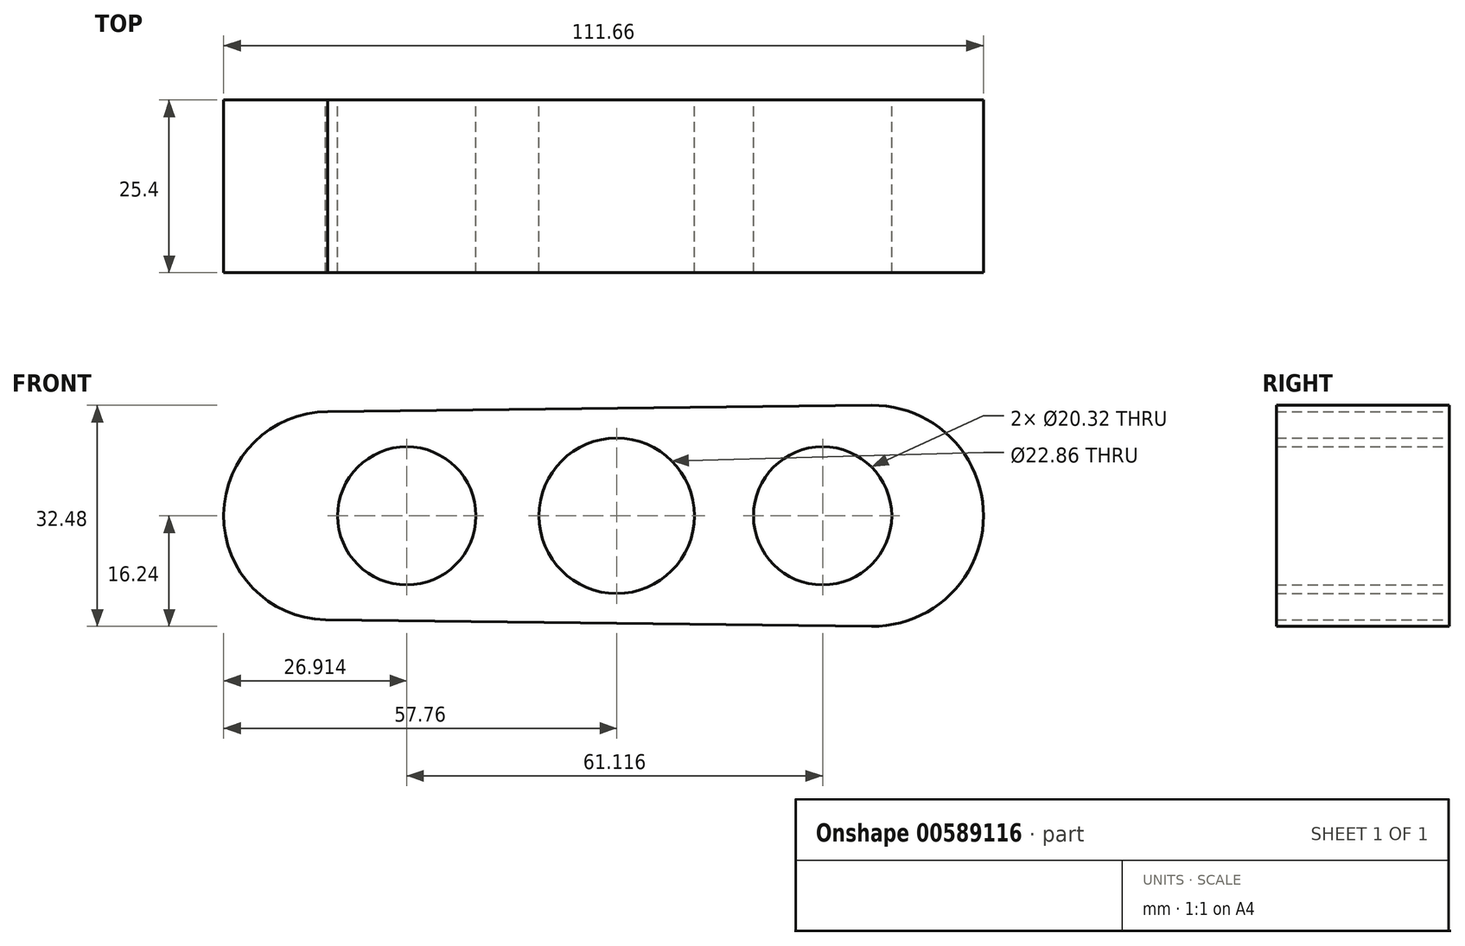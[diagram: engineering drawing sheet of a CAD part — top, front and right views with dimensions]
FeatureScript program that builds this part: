
annotation { "Feature Type Name" : "Feature", "Feature Type Description" : "" }
export const myFeature = defineFeature(function(context is Context, id is Id, definition is map)
    precondition{}
    {
        {
            var Q0;
            Q0=qCreatedBy(makeId("Front.planeOp"),FACE);
            var sketch = newSketch(context, id + "F0", { "sketchPlane" : qUnion([Q0])});
            skCircle(sketch, "E0", {"center": v(-42.45, 0) * mm, "radius": 15.3 * mm});
            skCircle(sketch, "E1", {"center": v(37.66, 0) * mm, "radius": 16.24 * mm});
            skLineSegment(sketch, "E2", {"start": v(-42.45, 15.3) * mm, "end": v(37.47, 16.24) * mm});
            skLineSegment(sketch, "E3", {"start": v(37.47, 16.24) * mm, "end": v(37.47, -16.24) * mm});
            skLineSegment(sketch, "E4", {"start": v(37.47, -16.24) * mm, "end": v(-42.81, -15.3) * mm});
            skLineSegment(sketch, "E5", {"start": v(-42.81, -15.3) * mm, "end": v(-42.45, 15.3) * mm});
            skSolve(sketch);
        }
        {
            var Q0;
            {var subQ0=sQuery(id+"F0.wireOp",EDGE,"E3");Q0=makeQuery(id+"F0.imprint","IMPRINT",FACE,{"disambiguationData":[TD([[makeQuery(id+"F0.imprint","IMPRINT",EDGE,{"derivedFrom":subQ0}),-1.0]])]});}
            var Q1;
            {var subQ0=sQuery(id+"F0.wireOp",EDGE,"E3");Q1=makeQuery(id+"F0.imprint","IMPRINT",FACE,{"disambiguationData":[TD([[makeQuery(id+"F0.imprint","IMPRINT",EDGE,{"derivedFrom":subQ0}),1.0]])]});}
            var Q2;
            {var subQ0=sQuery(id+"F0.wireOp",EDGE,"E2");Q2=makeQuery(id+"F0.imprint","IMPRINT",FACE,{"disambiguationData":[TD([[makeQuery(id+"F0.imprint","IMPRINT",EDGE,{"derivedFrom":subQ0}),-1.0]])]});}
            var Q3;
            {var subQ0=sQuery(id+"F0.wireOp",EDGE,"E5");Q3=makeQuery(id+"F0.imprint","IMPRINT",FACE,{"disambiguationData":[TD([[makeQuery(id+"F0.imprint","IMPRINT",EDGE,{"derivedFrom":subQ0}),-1.0]])]});}
            var Q4;
            {var subQ0=sQuery(id+"F0.wireOp",EDGE,"E5");Q4=makeQuery(id+"F0.imprint","IMPRINT",FACE,{"disambiguationData":[TD([[makeQuery(id+"F0.imprint","IMPRINT",EDGE,{"derivedFrom":subQ0}),1.0]])]});}
            extrude(context, id + "F1", {"entities" : qUnion([Q0, Q1, Q2, Q3, Q4]), "depth" : 25.4 * mm, "offsetDistance" : 25.4 * mm});
        }
        {
            var Q0;
            Q0=qCreatedBy(makeId("Front.planeOp"),FACE);
            var sketch = newSketch(context, id + "F2", { "sketchPlane" : qUnion([Q0])});
            skCircle(sketch, "E6", {"center": v(0, 0) * mm, "radius": 11.67 * mm});
            skCircle(sketch, "E7", {"center": v(-30.85, 0) * mm, "radius": 10.41 * mm});
            skCircle(sketch, "E8", {"center": v(30.27, 0) * mm, "radius": 10.41 * mm});
            skSolve(sketch);
        }
        {
            var Q0;
            Q0=sQuery(id+"F2.wireOp",VERTEX,"E7.center");
            var Q1;
            Q1=sQuery(id+"F2.wireOp",VERTEX,"E8.center");
            var Q2;
            Q2=makeQuery(id+"F1.opExtrude","SWEPT_BODY",BODY,{"disambiguationData":[OSD([sQuery(id+"F0.wireOp",EDGE,"E0"),sQuery(id+"F0.wireOp",EDGE,"E1"),sQuery(id+"F0.wireOp",EDGE,"E2"),sQuery(id+"F0.wireOp",EDGE,"E4")])]});
            hole(context, id + "F3", {"style" : HoleStyle.SIMPLE, "endStyle" : HoleEndStyle.THROUGH, "oppositeDirection" : true, "holeDiameter" : 20.32 * mm, "majorDiameter" : 6.35 * mm, "isTappedThrough" : true, "tappedDepth" : 12.7 * mm, "tapClearance" : 3, "locations" : qUnion([Q0, Q1]), "scope" : qUnion([Q2])});
        }
        {
            var Q0;
            Q0=makeQuery(id+"F1.opExtrude","CAP_FACE",FACE,{"disambiguationData":[OSD([sQuery(id+"F0.wireOp",EDGE,"E0"),sQuery(id+"F0.wireOp",EDGE,"E1"),sQuery(id+"F0.wireOp",EDGE,"E2"),sQuery(id+"F0.wireOp",EDGE,"E4")])],"isStart":true});
            var sketch = newSketch(context, id + "F4", { "sketchPlane" : qUnion([Q0])});
            skCircle(sketch, "E9", {"center": v(0, 0) * mm, "radius": 11.48 * mm});
            skSolve(sketch);
        }
        {
            var Q0;
            Q0=sQuery(id+"F4.wireOp",VERTEX,"E9.center");
            var Q1;
            Q1=makeQuery(id+"F1.opExtrude","SWEPT_BODY",BODY,{"disambiguationData":[OSD([sQuery(id+"F0.wireOp",EDGE,"E0"),sQuery(id+"F0.wireOp",EDGE,"E1"),sQuery(id+"F0.wireOp",EDGE,"E2"),sQuery(id+"F0.wireOp",EDGE,"E4")])]});
            hole(context, id + "F5", {"style" : HoleStyle.SIMPLE, "endStyle" : HoleEndStyle.THROUGH, "holeDiameter" : 22.86 * mm, "majorDiameter" : 6.35 * mm, "isTappedThrough" : true, "tappedDepth" : 12.7 * mm, "tapClearance" : 3, "locations" : qUnion([Q0]), "scope" : qUnion([Q1])});
        }
    });
